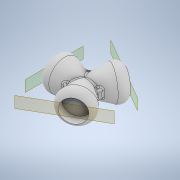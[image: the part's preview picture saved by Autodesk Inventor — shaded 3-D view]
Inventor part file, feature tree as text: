
AUTODESK INVENTOR PART (.ipt)
format: ipt  version: 2022 (Build 260153000, 153)  size: 549,376 bytes
history: native  units: mm
features: extrude x7, sketch x7, other x4, fillet x2
ambient origin geometry x8: Origin, YZ Plane, XZ Plane, XY Plane, X Axis, Y Axis, Z Axis, Center Point
bodies: Body1 (feature_tree)
feature tree (20):
  other  "Bryła1"
  extrude  "Wyciągnięcie proste1"  Depth=30.0mm
  other  "Płaszczyzna konstrukcyjna1"
  other  "Płaszczyzna konstrukcyjna2"
  other  "Płaszczyzna konstrukcyjna3"
  sketch  "Szkic9"
  sketch  "Szkic10"
  extrude  "Wyciągnięcie proste11"  Depth=30.0mm
  extrude  "Wyciągnięcie proste12"  Depth=30.0mm
  extrude  "Wyciągnięcie proste13"  TaperAngle=120.0deg  [1 undecoded]
  sketch  "Szkic12"
  sketch  "Szkic13"
  sketch  "Szkic14"
  extrude  "Wyciągnięcie proste14"  TaperAngle=120.0deg  [1 undecoded]
  extrude  "Wyciągnięcie proste15"  Depth=10.0mm TaperAngle=0.0deg
  extrude  "Wyciągnięcie proste16"  TaperAngle=60.0deg  [1 undecoded]
  fillet  "Zaokrąglenie1"  [1 undecoded]
  fillet  "Zaokrąglenie3"  [1 undecoded]
  sketch  "Szkic2"
  sketch  "Szkic11"
note: 5 required parameter values undecoded (feature->parameter linkage not recoverable at this tier; creation-order binding heuristic only, values carry confidence <= 0.55)
